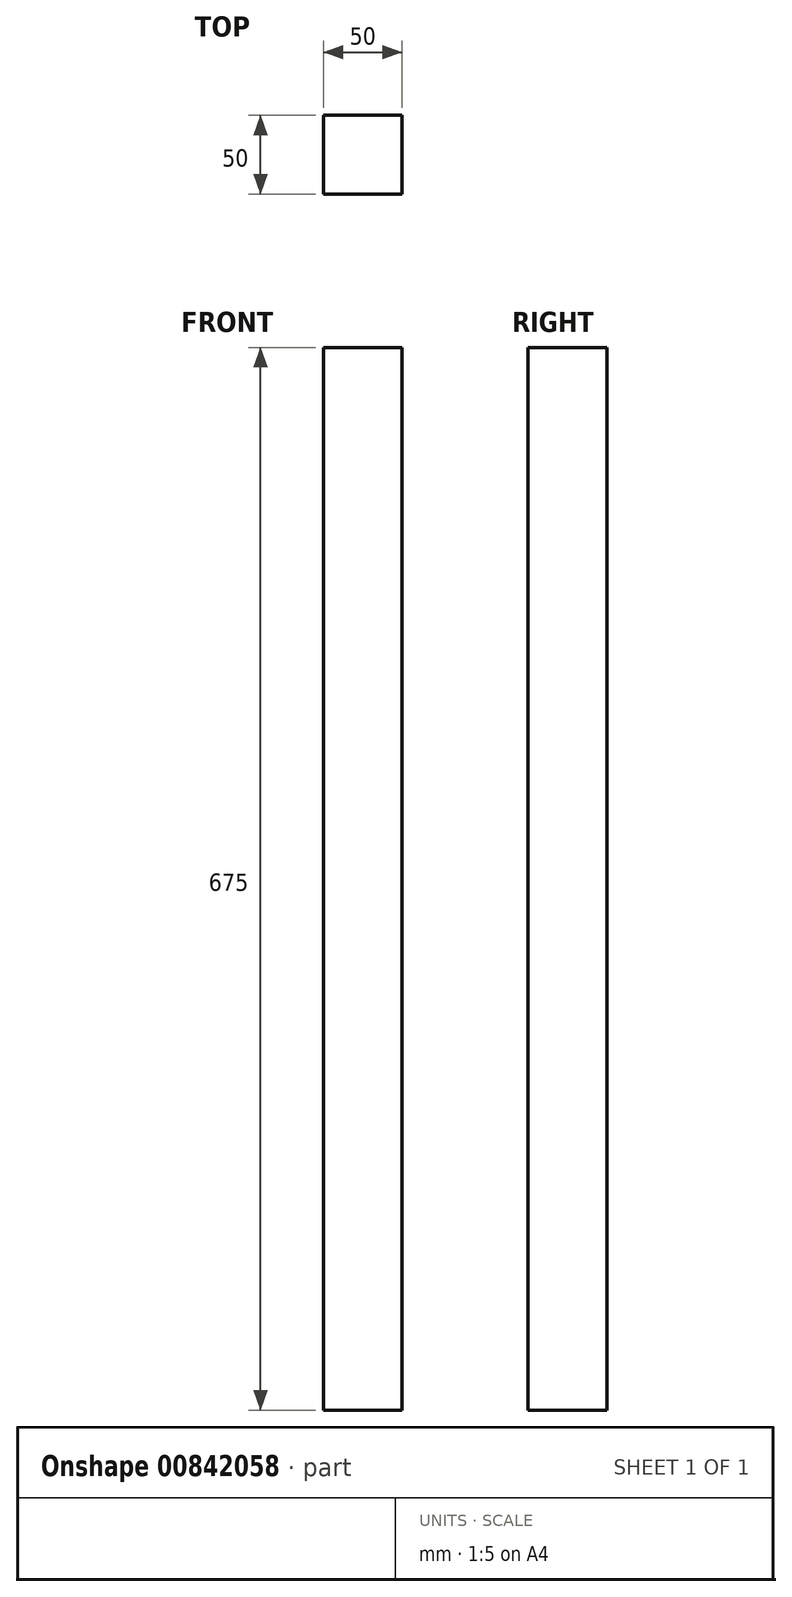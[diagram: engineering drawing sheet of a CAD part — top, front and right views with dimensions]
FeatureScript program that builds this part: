
annotation { "Feature Type Name" : "Feature", "Feature Type Description" : "" }
export const myFeature = defineFeature(function(context is Context, id is Id, definition is map)
    precondition{}
    {
        {
            var Q0;
            Q0=qCreatedBy(makeId("Top.planeOp"),FACE);
            var sketch = newSketch(context, id + "F0", { "sketchPlane" : qUnion([Q0])});
            skLineSegment(sketch, "E0.bottom", {"start": v(-101.37, 450) * mm, "end": v(-51.37, 450) * mm});
            skLineSegment(sketch, "E0.top", {"start": v(-101.37, 400) * mm, "end": v(-51.37, 400) * mm});
            skLineSegment(sketch, "E0.left", {"start": v(-101.37, 450) * mm, "end": v(-101.37, 400) * mm});
            skLineSegment(sketch, "E0.right", {"start": v(-51.37, 450) * mm, "end": v(-51.37, 400) * mm});
            skLineSegment(sketch, "E1.bottom", {"start": v(-101.37, 450) * mm, "end": v(398.63, 450) * mm});
            skLineSegment(sketch, "E1.top", {"start": v(-101.37, -50) * mm, "end": v(398.63, -50) * mm});
            skLineSegment(sketch, "E1.left", {"start": v(-101.37, 450) * mm, "end": v(-101.37, -50) * mm});
            skLineSegment(sketch, "E1.right", {"start": v(398.63, 450) * mm, "end": v(398.63, -50) * mm});
            skLineSegment(sketch, "E2.bottom", {"start": v(398.63, -50) * mm, "end": v(348.63, -50) * mm});
            skLineSegment(sketch, "E2.top", {"start": v(398.63, 0) * mm, "end": v(348.63, 0) * mm});
            skLineSegment(sketch, "E2.left", {"start": v(398.63, -50) * mm, "end": v(398.63, 0) * mm});
            skLineSegment(sketch, "E2.right", {"start": v(348.63, -50) * mm, "end": v(348.63, 0) * mm});
            skLineSegment(sketch, "E3.bottom", {"start": v(398.63, 450) * mm, "end": v(348.63, 450) * mm});
            skLineSegment(sketch, "E3.top", {"start": v(398.63, 400) * mm, "end": v(348.63, 400) * mm});
            skLineSegment(sketch, "E3.left", {"start": v(398.63, 450) * mm, "end": v(398.63, 400) * mm});
            skLineSegment(sketch, "E3.right", {"start": v(348.63, 450) * mm, "end": v(348.63, 400) * mm});
            skLineSegment(sketch, "E4.bottom", {"start": v(-101.37, -50) * mm, "end": v(-51.37, -50) * mm});
            skLineSegment(sketch, "E4.top", {"start": v(-101.37, 0) * mm, "end": v(-51.37, 0) * mm});
            skLineSegment(sketch, "E4.left", {"start": v(-101.37, -50) * mm, "end": v(-101.37, 0) * mm});
            skLineSegment(sketch, "E4.right", {"start": v(-51.37, -50) * mm, "end": v(-51.37, 0) * mm});
            skSolve(sketch);
        }
        {
            var Q0;
            Q0=makeQuery(id+"F0.imprint","IMPRINT",FACE,{"disambiguationData":[TD([[makeQuery(id+"F0.imprint","IMPRINT",EDGE,{"derivedFrom":sQuery(id+"F0.wireOp",EDGE,"E2.bottom")}),-1.0]])]});
            var Q1;
            Q1=makeQuery(id+"F0.imprint","IMPRINT",FACE,{"disambiguationData":[TD([[makeQuery(id+"F0.imprint","IMPRINT",EDGE,{"derivedFrom":sQuery(id+"F0.wireOp",EDGE,"E3.bottom")}),1.0]])]});
            var Q2;
            {var subQ0=sQuery(id+"F0.wireOp",EDGE,"E0.top");Q2=makeQuery(id+"F0.imprint","IMPRINT",FACE,{"disambiguationData":[TD([[makeQuery(id+"F0.imprint","IMPRINT",EDGE,{"derivedFrom":subQ0}),1.0]])]});}
            var Q3;
            Q3=makeQuery(id+"F0.imprint","IMPRINT",FACE,{"disambiguationData":[TD([[makeQuery(id+"F0.imprint","IMPRINT",EDGE,{"derivedFrom":sQuery(id+"F0.wireOp",EDGE,"E4.bottom")}),1.0]])]});
            extrude(context, id + "F1", {"entities" : qUnion([Q0, Q1, Q2, Q3]), "depth" : 675 * mm, "offsetDistance" : 25 * mm});
        }
    });
